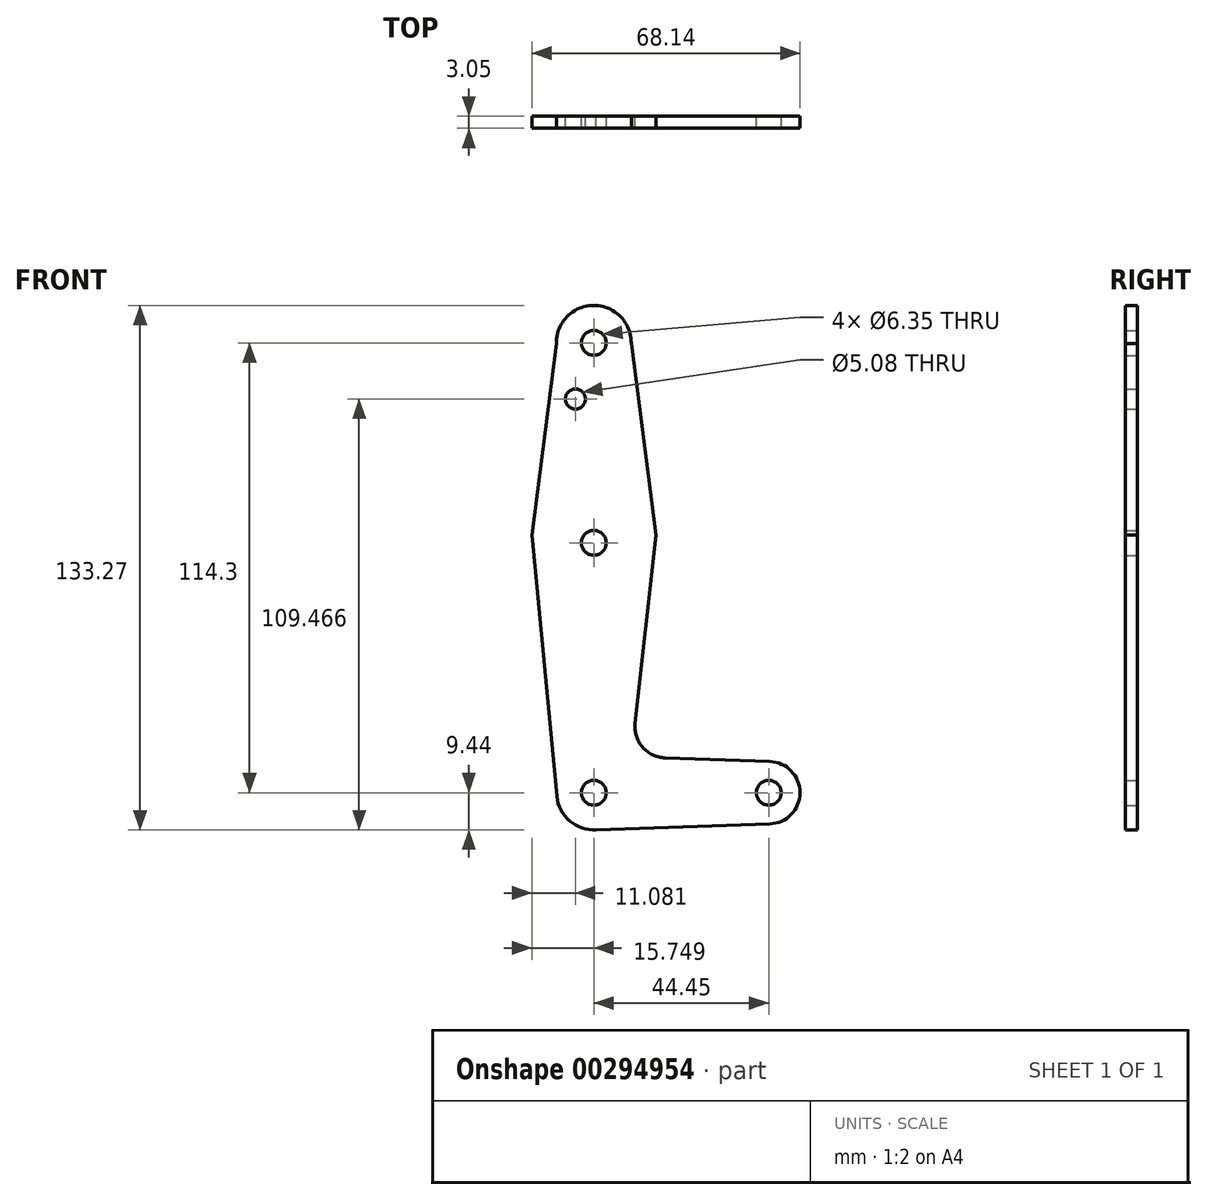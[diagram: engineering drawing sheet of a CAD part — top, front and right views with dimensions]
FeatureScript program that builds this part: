
annotation { "Feature Type Name" : "Feature", "Feature Type Description" : "" }
export const myFeature = defineFeature(function(context is Context, id is Id, definition is map)
    precondition{}
    {
        {
            var Q0;
            Q0=qCreatedBy(makeId("Front.planeOp"),FACE);
            var sketch = newSketch(context, id + "F0", { "sketchPlane" : qUnion([Q0])});
            skLineSegment(sketch, "E0", {"start": v(-32.62, 65.88) * mm, "end": v(-32.62, -38.98) * mm});
            skLineSegment(sketch, "E1", {"start": v(-32.62, -48.42) * mm, "end": v(-29.45, -48.42) * mm});
            skCircle(sketch, "E2", {"center": v(-32.62, 65.88) * mm, "radius": 9.53 * mm});
            skArc(sketch, "E3", {"start": v(-47.7, 10.12) * mm, "mid": v(-32.84, -0.8) * mm, "end": v(-17.68, 9.7) * mm});
            skCircle(sketch, "E4", {"center": v(11.83, -48.42) * mm, "radius": 7.94 * mm});
            skCircle(sketch, "E5", {"center": v(-32.62, -48.42) * mm, "radius": 9.44 * mm});
            skLineSegment(sketch, "E6", {"start": v(-42.14, 65.7) * mm, "end": v(-48.37, 17.1) * mm});
            skLineSegment(sketch, "E7", {"start": v(-23.45, 68.46) * mm, "end": v(-16.87, 17.1) * mm});
            skLineSegment(sketch, "E8", {"start": v(-48.37, 17.1) * mm, "end": v(-42.02, -49.32) * mm});
            skLineSegment(sketch, "E9", {"start": v(-16.87, 17.1) * mm, "end": v(-22.12, -30.78) * mm});
            skLineSegment(sketch, "E10", {"start": v(-14.48, -39.59) * mm, "end": v(12.1, -40.49) * mm});
            skLineSegment(sketch, "E11", {"start": v(-32.59, -57.86) * mm, "end": v(12.1, -56.35) * mm});
            skCircle(sketch, "E12", {"center": v(-32.62, 65.88) * mm, "radius": 3.18 * mm});
            skCircle(sketch, "E13", {"center": v(-32.62, 15.08) * mm, "radius": 3.18 * mm});
            skCircle(sketch, "E14", {"center": v(-32.62, -48.42) * mm, "radius": 3.18 * mm});
            skCircle(sketch, "E15", {"center": v(11.83, -48.42) * mm, "radius": 3.18 * mm});
            skArc(sketch, "E16.filletArc", {"start": v(-22.12, -30.78) * mm, "mid": v(-20.22, -36.85) * mm, "end": v(-14.48, -39.59) * mm});
            skCircle(sketch, "E17", {"center": v(-37.29, 51.6) * mm, "radius": 2.54 * mm});
            skArc(sketch, "E18.trimOffspring", {"start": v(-16.87, 17.1) * mm, "mid": v(-32.62, 30.96) * mm, "end": v(-48.37, 17.1) * mm});
            skLineSegment(sketch, "E19.trimOffspring", {"start": v(-23.18, -48.42) * mm, "end": v(11.83, -48.42) * mm});
            skLineSegment(sketch, "E20.trimOffspring", {"start": v(-32.62, -45.24) * mm, "end": v(-32.62, -48.42) * mm});
            skSolve(sketch);
        }
        {
            var Q0;
            Q0 = qSketchRegion(id + "F0", true);
            extrude(context, id + "F1", {"entities" : qUnion([Q0]), "depth" : 3.05 * mm});
        }
    });
